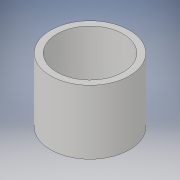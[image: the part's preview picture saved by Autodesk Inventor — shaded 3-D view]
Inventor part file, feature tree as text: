
AUTODESK INVENTOR PART (.ipt)
format: ipt  version: 2018 (Build 220112000, 112)  size: 110,592 bytes
history: native  units: in
note: dims shown in document units (in); Inventor stores cm internally (conversion verified against a paired STEP export)
features: revolve x1, sketch x1
ambient origin geometry x8: Origin, YZ Plane, XZ Plane, XY Plane, X Axis, Y Axis, Z Axis, Center Point
bodies: Solid1 (feature_tree)
feature tree (2):
  revolve  "Revolution1"  [1 undecoded]
  sketch  "Sketch1"  dims[d0=61.0236in d1=72.8346in d2=0.0in d3=118.1102in d4=90.0deg]
note: 1 required parameter value undecoded (feature->parameter linkage not recoverable at this tier; creation-order binding heuristic only, values carry confidence <= 0.55)
